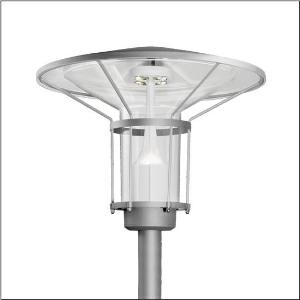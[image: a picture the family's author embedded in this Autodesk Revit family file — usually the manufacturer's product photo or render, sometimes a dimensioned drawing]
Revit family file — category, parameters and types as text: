
# Revit family: laterne_classic_iq___pl1_2s_5xa5245rf14h_f81d
name_source: partatom
category: Lighting Fixtures
units: mm (PartAtom-declared; Revit-internal decimal feet)

## family parameters
Cut with Voids When Loaded = No
Host = Face
Light Source = No
Part Type = Normal
Room Calculation Point = No
Round Connector Dimension = Use Diameter
Shared = No

## types (1)
- --- (1 x LED, 2670 lm, 18.5 W, 4000K)
    Apparent Load = 19 VA
    CIE Flux Codes = 21 60 93 97 100
    Color Rendering = 70
    Color Temperature = 4000K
    Default Elevation = 1800 mm
    Description = Lantern Classic iQ, mast luminaire, Module 540 iQ-SR, primary light control with 3 zone facetted reflector, of plastic, silver coated, highly specular, structured, primary optical cover: cover, of PMMA, transparent, light distribution: PL1.2s, light emission: direct distribution, primary light characteristic: symmetric, installation type: post-top, LED, High Power LED, rated luminous flux: 2.670lm, luminous efficacy: 144lm/W, light colour: 740, colour temperature: 4000K, control gear: ECG iQ, control: presetting dimming logarithmic, Street-Remote, Auto-Match, Temp-Guard, Lumen-Switch, Night-Set, Smart-Wire, Light-Fading, Desk-Remote (wireless, voltage-free reading and setting of iQ features in the workshop via application-optimized NFC function/RFID function), optimised constant luminous flux control (CLO 2.0), with terminal, 6-pole, max. 2.5mm², mains connection: 230..240V, AC, 50/60Hz, start of lifetime: 19W, end of service life: 20W, reduction: 9W, luminaire housing, upper part, of glass-fibre reinforced polyester, coated, Siteco® metallic grey (DB 702S), diameter: 750mm, height: 596mm, spigot size: d x l = 76 x 70mm (post-top) | with reducer (optional accessory) 60 x 70mm, post-top mast mounting element, of diecast aluminium, coated, Siteco® metallic grey (DB 702S), Module 540 iQ-SR, traffic white (RAL 9016), equipment: standard, protection rating (complete): IP65, insulation class (complete): insulation class II (safety insulation), certification: CE, ENEC, VDE, packaging unit: 1 piece

Light Distribution: PL1.2s
    Height = 596 mm
    Lamp = 1 x LED
    Lamp Light Flux = 2670 lm
    Lamp Power = 18.5 W
    Lamp count = 1
    Length = 750 mm
    Luminous efficacy = 144 lm/W
    Manufacturer = Siteco
    ModVariant = No
    Model = 5XA5245RF14H
    Number of Poles = 1
    OnlyDefault = Yes
    Power Factor = 1
    Product Name = Laterne Classic iQ | PL1.2s
    Product group = mast luminaire | pylon top
    ProductGroupID = 6100
    Protection Class = Protection class II
    Protection Degree = IP 65
    RLX_Detail_Level = 1
    RLX_Emergency_Light_Flux = 0 lm
    RLX_Emergency_Type = 0
    RLX_Emergency_Type_DB = No
    RlxData = <blob elided: 62877 chars, md5=e6de675b>
    Socket = socket
    Standby Power = 0 W
    System Light Flux = 2670 lm
    System Power = 19 W
    Type Comments = factory setting: luminous flux: 100 % | dim-lin: 254 | 385 mA
    Type Image = l_1006052.jpg
    URL = http://relux.com
    VarID = @adj_095271
    Voltage = 0 V
    Weight = 0.00 kg
    Width = 0 mm  [stored 0 ft]

note: [stored X ft] marks values corroborated as IEEE doubles in the binary element streams (Revit-internal decimal feet)

## geometry (parser evidence)
native form markers: Blend x4, Sweep x10
no freeform markers — native parametric forms only
